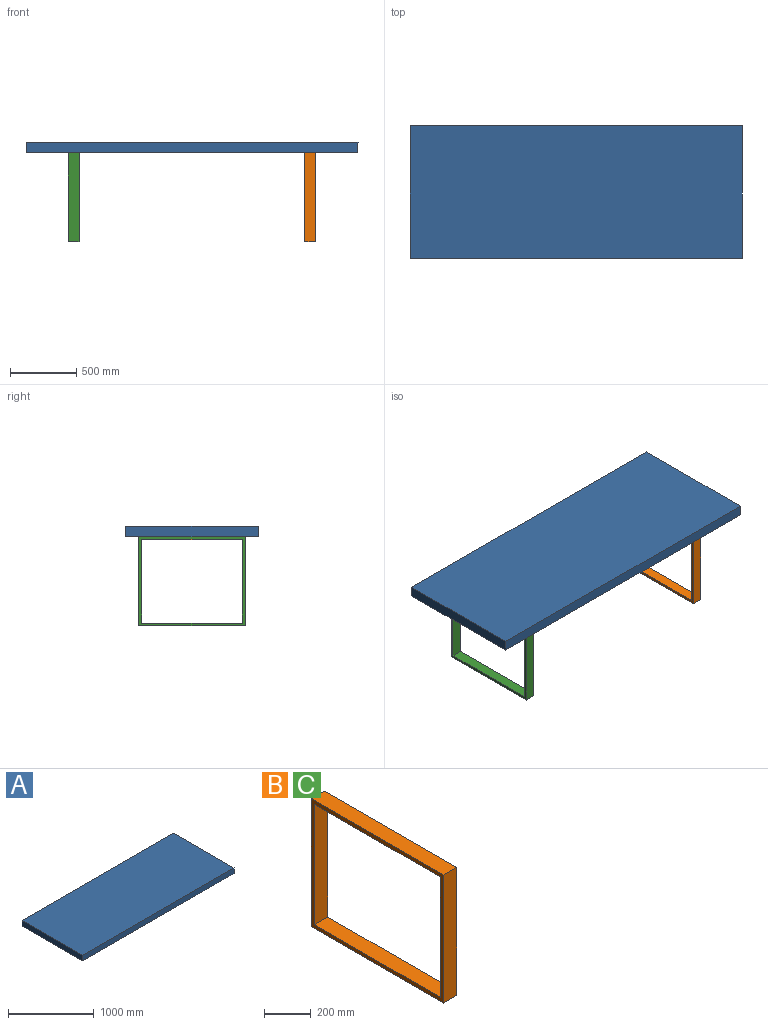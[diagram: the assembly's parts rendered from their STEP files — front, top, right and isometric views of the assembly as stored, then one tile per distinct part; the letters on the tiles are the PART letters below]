
ASSEMBLY  parts=3 mates=2
PART A: 6 faces, bbox 2500x1000x80 mm
  f0: plane 2500x80mm, normal (0,-1,0), area 200000mm2, adj f1,f3,f4,f5
  f1: plane 1000x80mm, normal (1,0,0), area 80000mm2, adj f0,f2,f4,f5
  f2: plane 2500x80mm, normal (0,1,0), area 200000mm2, adj f1,f3,f4,f5
  f3: plane 1000x80mm, normal (-1,0,0), area 80000mm2, adj f0,f2,f4,f5
  f4: plane 2500x1000mm, normal (0,0,1), area 2500000mm2, adj f0,f1,f2,f3
  f5: plane 2500x1000mm, normal (0,0,-1), area 2500000mm2, adj f0,f1,f2,f3
PART B: 10 faces, bbox 80x800x670 mm
  f0: plane 670x80mm, normal (0,1,0), area 53600mm2, adj f1,f7,f8,f9
  f1: plane 800x80mm, normal (0,0,1), area 64000mm2, adj f0,f2,f8,f9
  f2: plane 670x80mm, normal (0,-1,0), area 53600mm2, adj f1,f7,f8,f9
  f3: plane 630x80mm, normal (0,-1,0), area 50400mm2, adj f4,f6,f8,f9
  f4: plane 760x80mm, normal (0,0,1), area 60800mm2, adj f3,f5,f8,f9
  f5: plane 630x80mm, normal (0,1,0), area 50400mm2, adj f4,f6,f8,f9
  f6: plane 760x80mm, normal (0,0,-1), area 60800mm2, adj f3,f5,f8,f9
  f7: plane 800x80mm, normal (0,0,-1), area 64000mm2, adj f0,f2,f8,f9
  f8: plane 800x670mm, normal (1,0,0), area 57200mm2, adj f0,f1,f2,f3,f4,f5,f6,f7
  f9: plane 800x670mm, normal (-1,0,0), area 57200mm2, adj f0,f1,f2,f3,f4,f5,f6,f7
PART C: same geometry as B
PLACE A rot(axis=(0,-1,0),180deg) t=(-80.11,4.28,47.74)mm
PLACE B rot(axis=(0,0,1),180deg) t=(849.59,4.28,-367.92)mm
PLACE C rot(axis=(0,0,1),180deg) t=(-930.41,4.28,-366.65)mm
MATE fastened C.f1 <-> A.f4  axis (0,0,1) through (-970.17,4.28,-31.62)mm
MATE fastened B.f1 <-> A.f4  axis (0,0,1) through (809.83,4.28,-32.9)mm
